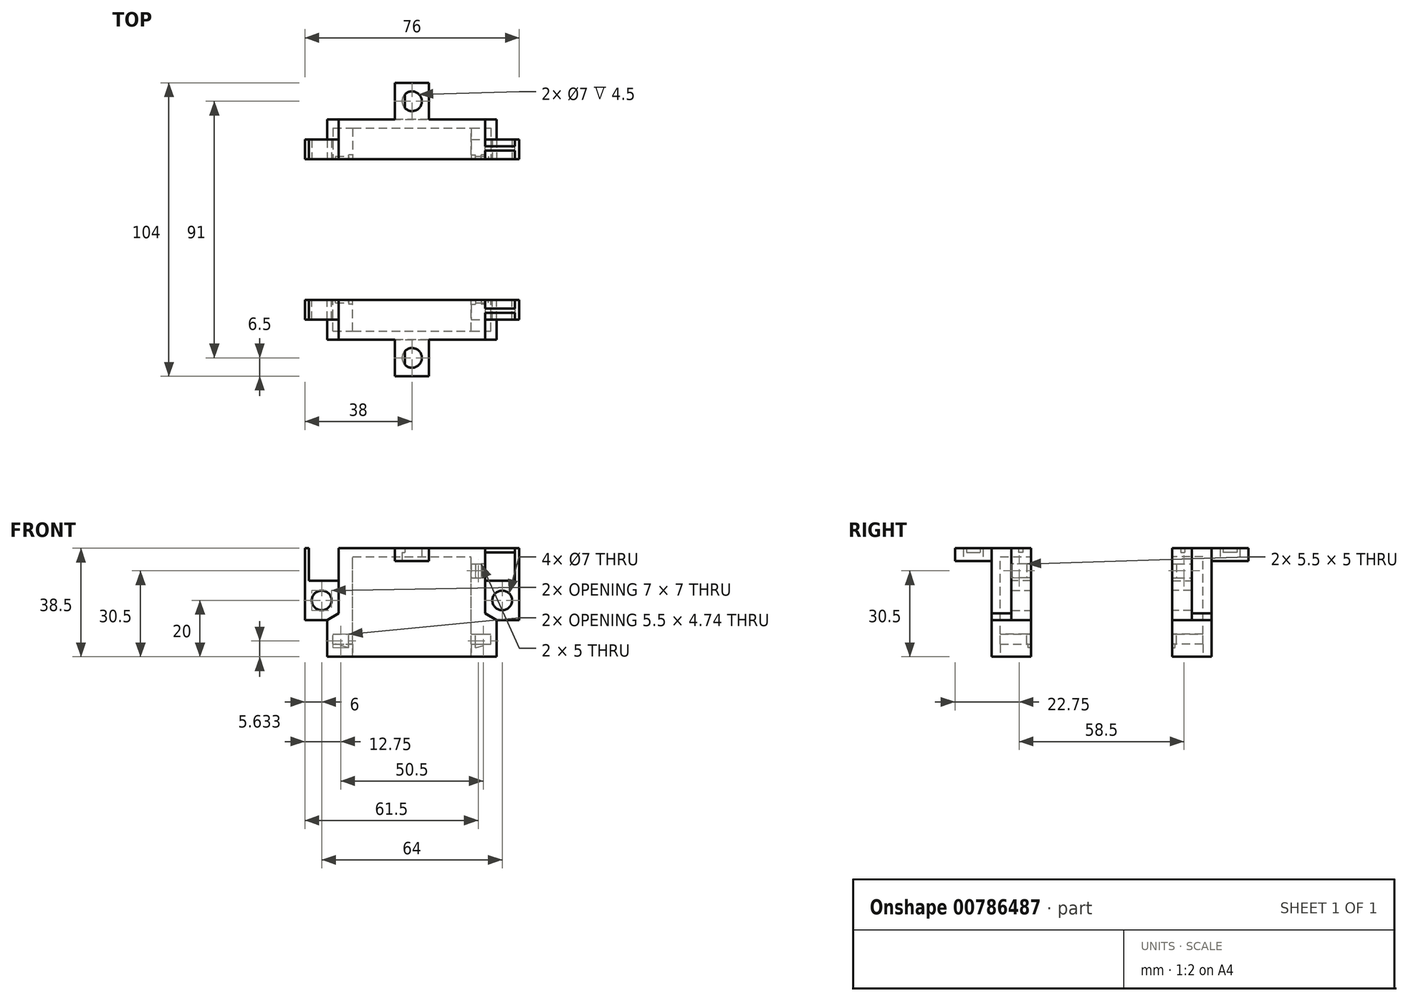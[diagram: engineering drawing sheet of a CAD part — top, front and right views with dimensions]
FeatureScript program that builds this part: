
annotation { "Feature Type Name" : "Feature", "Feature Type Description" : "" }
export const myFeature = defineFeature(function(context is Context, id is Id, definition is map)
    precondition{}
    {
        {
            var Q0;
            Q0=qCreatedBy(makeId("Top.planeOp"),FACE);
            var sketch = newSketch(context, id + "F0", { "sketchPlane" : qUnion([Q0])});
            skLineSegment(sketch, "E0.bottom", {"start": v(-30, 7) * mm, "end": v(30, 7) * mm});
            skLineSegment(sketch, "E0.top", {"start": v(-30, -7) * mm, "end": v(30, -7) * mm});
            skLineSegment(sketch, "E0.left", {"start": v(-30, 7) * mm, "end": v(-30, -7) * mm});
            skLineSegment(sketch, "E0.right", {"start": v(30, 7) * mm, "end": v(30, -7) * mm});
            skSolve(sketch);
        }
        {
            var Q0;
            Q0=qSketchRegion(id+"F0",true);
            extrude(context, id + "F1", {"entities" : qUnion([Q0]), "depth" : 36 * mm, "offsetDistance" : 25 * mm});
        }
        {
            var Q0;
            Q0=makeQuery(id+"F1.opExtrude","CAP_FACE",FACE,{"disambiguationData":[OSD([sQuery(id+"F0.wireOp",EDGE,"E0.bottom"),sQuery(id+"F0.wireOp",EDGE,"E0.top"),sQuery(id+"F0.wireOp",EDGE,"E0.left"),sQuery(id+"F0.wireOp",EDGE,"E0.right")])],"isStart":false});
            cPlane(context, id + "F2", {"entities" : qUnion([Q0]), "cplaneType" : CPlaneType.OFFSET, "offset" : 3 * mm, "oppositeDirection" : true, "width" : 150 * mm, "height" : 150 * mm});
        }
        {
            var Q0;
            Q0=qCreatedBy(id+"F2.planeOp",FACE);
            var sketch = newSketch(context, id + "F3", { "sketchPlane" : qUnion([Q0])});
            skLineSegment(sketch, "E1.bottom", {"start": v(-21, 7) * mm, "end": v(21, 7) * mm});
            skLineSegment(sketch, "E1.top", {"start": v(-21, -4) * mm, "end": v(21, -4) * mm});
            skLineSegment(sketch, "E1.left", {"start": v(-21, 7) * mm, "end": v(-21, -4) * mm});
            skLineSegment(sketch, "E1.right", {"start": v(21, 7) * mm, "end": v(21, -4) * mm});
            skSolve(sketch);
        }
        {
            var Q0;
            Q0=qSketchRegion(id+"F3",true);
            extrude(context, id + "F4", {"entities" : qUnion([Q0]), "operationType" : NewBodyOperationType.REMOVE, "oppositeDirection" : true, "depth" : 25 * mm, "offsetDistance" : 25 * mm});
        }
        {
            var Q0;
            Q0=makeQuery(id+"F1.opExtrude","SWEPT_FACE",FACE,{"disambiguationData":[OSD([sQuery(id+"F0.wireOp",EDGE,"E0.bottom")])]});
            var sketch = newSketch(context, id + "F5", { "sketchPlane" : qUnion([Q0])});
            skLineSegment(sketch, "E2.bottom", {"start": v(28, 4.5) * mm, "end": v(-28, 4.5) * mm});
            skLineSegment(sketch, "E2.top", {"start": v(28, 8) * mm, "end": v(-28, 8) * mm});
            skLineSegment(sketch, "E2.left", {"start": v(28, 4.5) * mm, "end": v(28, 8) * mm});
            skLineSegment(sketch, "E2.right", {"start": v(-28, 4.5) * mm, "end": v(-28, 8) * mm});
            skLineSegment(sketch, "E3.bottom", {"start": v(21, 4.5) * mm, "end": v(-21, 4.5) * mm});
            skLineSegment(sketch, "E3.top", {"start": v(21, 0) * mm, "end": v(-21, 0) * mm});
            skLineSegment(sketch, "E3.left", {"start": v(21, 4.5) * mm, "end": v(21, 0) * mm});
            skLineSegment(sketch, "E3.right", {"start": v(-21, 4.5) * mm, "end": v(-21, 0) * mm});
            skSolve(sketch);
        }
        {
            var Q0;
            {var subQ9=sQuery(id+"F5.wireOp",EDGE,"E2.left");Q0=qUnion([makeQuery(id+"F5.imprint","IMPRINT",FACE,{"disambiguationData":[TD([[makeQuery(id+"F5.imprint","IMPRINT",EDGE,{"derivedFrom":subQ9}),1.0]])]}),makeQuery(id+"F5.imprint","IMPRINT",FACE,{"disambiguationData":[TD([[makeQuery(id+"F5.imprint","IMPRINT",EDGE,{"derivedFrom":sQuery(id+"F5.wireOp",EDGE,"E3.top")}),-1.0]])]})]);}
            extrude(context, id + "F6", {"entities" : qUnion([Q0]), "operationType" : NewBodyOperationType.REMOVE, "oppositeDirection" : true, "depth" : 11 * mm, "offsetDistance" : 25 * mm});
        }
        {
            var Q0;
            Q0=makeQuery(id+"F1.opExtrude","SWEPT_FACE",FACE,{"disambiguationData":[OSD([sQuery(id+"F0.wireOp",EDGE,"E0.bottom")])]});
            var sketch = newSketch(context, id + "F7", { "sketchPlane" : qUnion([Q0])});
            skLineSegment(sketch, "E4.bottom", {"start": v(30, 13) * mm, "end": v(38, 13) * mm});
            skLineSegment(sketch, "E4.top", {"start": v(30, 27) * mm, "end": v(38, 27) * mm});
            skLineSegment(sketch, "E4.left", {"start": v(30, 13) * mm, "end": v(30, 27) * mm});
            skLineSegment(sketch, "E4.right", {"start": v(38, 13) * mm, "end": v(38, 27) * mm});
            skLineSegment(sketch, "E5.MirrorCS", {"start": v(-38, 13) * mm, "end": v(-38, 27) * mm});
            skLineSegment(sketch, "E6.MirrorCS", {"start": v(-30, 13) * mm, "end": v(-38, 13) * mm});
            skLineSegment(sketch, "E7.MirrorCS", {"start": v(-30, 13) * mm, "end": v(-30, 27) * mm});
            skLineSegment(sketch, "E8.MirrorCS", {"start": v(-30, 27) * mm, "end": v(-38, 27) * mm});
            skSolve(sketch);
        }
        {
            var Q0;
            Q0=qSketchRegion(id+"F7",true);
            extrude(context, id + "F8", {"entities" : qUnion([Q0]), "operationType" : NewBodyOperationType.ADD, "oppositeDirection" : true, "depth" : 14 * mm, "offsetDistance" : 25 * mm});
        }
        {
            var Q0;
            Q0=makeQuery(id+"F8.boolean.opBoolean","MERGE",FACE,{"derivedFrom":[makeQuery(id+"F1.opExtrude","SWEPT_FACE",FACE,{"disambiguationData":[OSD([sQuery(id+"F0.wireOp",EDGE,"E0.bottom")])]}),makeQuery(id+"F8.opExtrude","CAP_FACE",FACE,{"disambiguationData":[OSD([sQuery(id+"F7.wireOp",EDGE,"E4.bottom"),sQuery(id+"F7.wireOp",EDGE,"E4.top"),sQuery(id+"F7.wireOp",EDGE,"E4.left"),sQuery(id+"F7.wireOp",EDGE,"E4.right")])],"isStart":true}),makeQuery(id+"F8.opExtrude","CAP_FACE",FACE,{"disambiguationData":[OSD([sQuery(id+"F7.wireOp",EDGE,"E5.MirrorCS"),sQuery(id+"F7.wireOp",EDGE,"E6.MirrorCS"),sQuery(id+"F7.wireOp",EDGE,"E7.MirrorCS"),sQuery(id+"F7.wireOp",EDGE,"E8.MirrorCS")])],"isStart":true})]});
            var sketch = newSketch(context, id + "F9", { "sketchPlane" : qUnion([Q0])});
            skCircle(sketch, "E9", {"center": v(32, 20) * mm, "radius": 3.5 * mm});
            skCircle(sketch, "E10.MirrorC", {"center": v(-32, 20) * mm, "radius": 3.5 * mm});
            skSolve(sketch);
        }
        {
            var Q0;
            Q0=qSketchRegion(id+"F9",true);
            extrude(context, id + "F10", {"entities" : qUnion([Q0]), "operationType" : NewBodyOperationType.REMOVE, "oppositeDirection" : true, "depth" : 14 * mm, "offsetDistance" : 25 * mm});
        }
        {
            var Q0;
            Q0=makeQuery(id+"F8.boolean.opBoolean","MERGE",FACE,{"derivedFrom":[makeQuery(id+"F1.opExtrude","SWEPT_FACE",FACE,{"disambiguationData":[OSD([sQuery(id+"F0.wireOp",EDGE,"E0.top")])]}),makeQuery(id+"F8.opExtrude","CAP_FACE",FACE,{"disambiguationData":[OSD([sQuery(id+"F7.wireOp",EDGE,"E4.bottom"),sQuery(id+"F7.wireOp",EDGE,"E4.top"),sQuery(id+"F7.wireOp",EDGE,"E4.left"),sQuery(id+"F7.wireOp",EDGE,"E4.right")])],"isStart":false}),makeQuery(id+"F8.opExtrude","CAP_FACE",FACE,{"disambiguationData":[OSD([sQuery(id+"F7.wireOp",EDGE,"E5.MirrorCS"),sQuery(id+"F7.wireOp",EDGE,"E6.MirrorCS"),sQuery(id+"F7.wireOp",EDGE,"E7.MirrorCS"),sQuery(id+"F7.wireOp",EDGE,"E8.MirrorCS")])],"isStart":false})]});
            var sketch = newSketch(context, id + "F11", { "sketchPlane" : qUnion([Q0])});
            skLineSegment(sketch, "E11.bottom", {"start": v(38, 13) * mm, "end": v(26, 13) * mm});
            skLineSegment(sketch, "E11.top", {"start": v(38, 27) * mm, "end": v(26, 27) * mm});
            skLineSegment(sketch, "E11.left", {"start": v(38, 13) * mm, "end": v(38, 27) * mm});
            skLineSegment(sketch, "E11.right", {"start": v(26, 13) * mm, "end": v(26, 27) * mm});
            skLineSegment(sketch, "E12.MirrorCS", {"start": v(-38, 13) * mm, "end": v(-26, 13) * mm});
            skLineSegment(sketch, "E13.MirrorCS", {"start": v(-26, 13) * mm, "end": v(-26, 27) * mm});
            skLineSegment(sketch, "E14.MirrorCS", {"start": v(-38, 13) * mm, "end": v(-38, 27) * mm});
            skLineSegment(sketch, "E15.MirrorCS", {"start": v(-38, 27) * mm, "end": v(-26, 27) * mm});
            skSolve(sketch);
        }
        {
            var Q0;
            Q0=qSketchRegion(id+"F11",true);
            extrude(context, id + "F12", {"entities" : qUnion([Q0]), "operationType" : NewBodyOperationType.REMOVE, "oppositeDirection" : true, "depth" : 7 * mm, "offsetDistance" : 25 * mm});
        }
        {
            var Q0;
            Q0=makeQuery(id+"F8.boolean.opBoolean","MERGE",FACE,{"derivedFrom":[makeQuery(id+"F1.opExtrude","SWEPT_FACE",FACE,{"disambiguationData":[OSD([sQuery(id+"F0.wireOp",EDGE,"E0.top")])]}),makeQuery(id+"F8.opExtrude","CAP_FACE",FACE,{"disambiguationData":[OSD([sQuery(id+"F7.wireOp",EDGE,"E4.bottom"),sQuery(id+"F7.wireOp",EDGE,"E4.top"),sQuery(id+"F7.wireOp",EDGE,"E4.left"),sQuery(id+"F7.wireOp",EDGE,"E4.right")])],"isStart":false}),makeQuery(id+"F8.opExtrude","CAP_FACE",FACE,{"disambiguationData":[OSD([sQuery(id+"F7.wireOp",EDGE,"E5.MirrorCS"),sQuery(id+"F7.wireOp",EDGE,"E6.MirrorCS"),sQuery(id+"F7.wireOp",EDGE,"E7.MirrorCS"),sQuery(id+"F7.wireOp",EDGE,"E8.MirrorCS")])],"isStart":false})]});
            var sketch = newSketch(context, id + "F13", { "sketchPlane" : qUnion([Q0])});
            skLineSegment(sketch, "E16.bottom", {"start": v(30, 36) * mm, "end": v(26, 36) * mm});
            skLineSegment(sketch, "E16.top", {"start": v(30, 27) * mm, "end": v(26, 27) * mm});
            skLineSegment(sketch, "E16.left", {"start": v(30, 36) * mm, "end": v(30, 27) * mm});
            skLineSegment(sketch, "E16.right", {"start": v(26, 36) * mm, "end": v(26, 27) * mm});
            skLineSegment(sketch, "E17.bottom", {"start": v(-30, 36) * mm, "end": v(-26, 36) * mm});
            skLineSegment(sketch, "E17.top", {"start": v(-30, 27) * mm, "end": v(-26, 27) * mm});
            skLineSegment(sketch, "E17.left", {"start": v(-30, 36) * mm, "end": v(-30, 27) * mm});
            skLineSegment(sketch, "E17.right", {"start": v(-26, 36) * mm, "end": v(-26, 27) * mm});
            skSolve(sketch);
        }
        {
            var Q0;
            Q0=qSketchRegion(id+"F13",true);
            extrude(context, id + "F14", {"entities" : qUnion([Q0]), "operationType" : NewBodyOperationType.REMOVE, "oppositeDirection" : true, "depth" : 14 * mm, "offsetDistance" : 25 * mm});
        }
        {
            var Q0;
            Q0=makeQuery(id+"F14.boolean.opBoolean","MERGE",FACE,{"derivedFrom":[makeQuery(id+"F12.boolean.opBoolean","COPY",FACE,{"derivedFrom":makeQuery(id+"F12.opExtrude","SWEPT_FACE",FACE,{"disambiguationData":[OSD([sQuery(id+"F11.wireOp",EDGE,"E11.right")])]})}),makeQuery(id+"F14.opExtrude","SWEPT_FACE",FACE,{"disambiguationData":[OSD([sQuery(id+"F13.wireOp",EDGE,"E16.right")])]})]});
            var sketch = newSketch(context, id + "F15", { "sketchPlane" : qUnion([Q0])});
            skLineSegment(sketch, "E18.bottom", {"start": v(7, 33) * mm, "end": v(0, 33) * mm});
            skLineSegment(sketch, "E18.top", {"start": v(7, 28) * mm, "end": v(0, 28) * mm});
            skLineSegment(sketch, "E18.left", {"start": v(7, 33) * mm, "end": v(7, 28) * mm});
            skLineSegment(sketch, "E18.right", {"start": v(0, 33) * mm, "end": v(0, 28) * mm});
            skSolve(sketch);
        }
        {
            var Q0;
            Q0=qSketchRegion(id+"F15",true);
            extrude(context, id + "F16", {"entities" : qUnion([Q0]), "operationType" : NewBodyOperationType.REMOVE, "oppositeDirection" : true, "depth" : 5 * mm, "offsetDistance" : 25 * mm});
        }
        {
            var Q0;
            {var subQ0=sQuery(id+"F7.wireOp",EDGE,"E8.MirrorCS");var subQ1=sQuery(id+"F7.wireOp",EDGE,"E5.MirrorCS");var subQ3=sQuery(id+"F0.wireOp",EDGE,"E0.bottom");var subQ4=makeQuery(id+"F1.opExtrude","SWEPT_FACE",FACE,{"disambiguationData":[OSD([subQ3])]});var subQ10=sQuery(id+"F0.wireOp",EDGE,"E0.right");var subQ11=sQuery(id+"F7.wireOp",EDGE,"E6.MirrorCS");Q0=makeQuery(id+"F16.boolean.opBoolean","SPLIT",FACE,{"disambiguationData":[TD([makeQuery(id+"F1.opExtrude","SWEPT_FACE",FACE,{"disambiguationData":[OSD([subQ10])]})])],"derivedFrom":makeQuery(id+"F8.boolean.opBoolean","MERGE",FACE,{"derivedFrom":[subQ4,makeQuery(id+"F8.opExtrude","CAP_FACE",FACE,{"disambiguationData":[OSD([sQuery(id+"F7.wireOp",EDGE,"E4.bottom"),sQuery(id+"F7.wireOp",EDGE,"E4.top"),sQuery(id+"F7.wireOp",EDGE,"E4.left"),sQuery(id+"F7.wireOp",EDGE,"E4.right")])],"isStart":true}),makeQuery(id+"F8.opExtrude","CAP_FACE",FACE,{"disambiguationData":[OSD([subQ1,subQ11,sQuery(id+"F7.wireOp",EDGE,"E7.MirrorCS"),subQ0])],"isStart":true})]})});}
            var sketch = newSketch(context, id + "F17", { "sketchPlane" : qUnion([Q0])});
            skLineSegment(sketch, "E19", {"start": v(-21, 2.86) * mm, "end": v(-27.1, 4.5) * mm});
            skLineSegment(sketch, "E20", {"start": v(-27.1, 4.5) * mm, "end": v(-21, 4.5) * mm});
            skLineSegment(sketch, "E21", {"start": v(-21, 4.5) * mm, "end": v(-21, 2.86) * mm});
            skLineSegment(sketch, "E22.MirrorCS", {"start": v(21, 2.86) * mm, "end": v(27.1, 4.5) * mm});
            skLineSegment(sketch, "E23.MirrorCS", {"start": v(21, 4.5) * mm, "end": v(21, 2.86) * mm});
            skLineSegment(sketch, "E24.MirrorCS", {"start": v(27.1, 4.5) * mm, "end": v(21, 4.5) * mm});
            skSolve(sketch);
        }
        {
            var Q0;
            Q0=qSketchRegion(id+"F17",true);
            extrude(context, id + "F18", {"entities" : qUnion([Q0]), "operationType" : NewBodyOperationType.REMOVE, "oppositeDirection" : true, "depth" : 1 * mm, "offsetDistance" : 25 * mm});
        }
        {
            var Q0;
            Q0=makeQuery(id+"F8.boolean.opBoolean","MERGE",FACE,{"derivedFrom":[makeQuery(id+"F1.opExtrude","SWEPT_FACE",FACE,{"disambiguationData":[OSD([sQuery(id+"F0.wireOp",EDGE,"E0.top")])]}),makeQuery(id+"F8.opExtrude","CAP_FACE",FACE,{"disambiguationData":[OSD([sQuery(id+"F7.wireOp",EDGE,"E4.bottom"),sQuery(id+"F7.wireOp",EDGE,"E4.top"),sQuery(id+"F7.wireOp",EDGE,"E4.left"),sQuery(id+"F7.wireOp",EDGE,"E4.right")])],"isStart":false}),makeQuery(id+"F8.opExtrude","CAP_FACE",FACE,{"disambiguationData":[OSD([sQuery(id+"F7.wireOp",EDGE,"E5.MirrorCS"),sQuery(id+"F7.wireOp",EDGE,"E6.MirrorCS"),sQuery(id+"F7.wireOp",EDGE,"E7.MirrorCS"),sQuery(id+"F7.wireOp",EDGE,"E8.MirrorCS")])],"isStart":false})]});
            var sketch = newSketch(context, id + "F19", { "sketchPlane" : qUnion([Q0])});
            skLineSegment(sketch, "E25.bottom", {"start": v(6, 36) * mm, "end": v(-6, 36) * mm});
            skLineSegment(sketch, "E25.top", {"start": v(6, 31) * mm, "end": v(-6, 31) * mm});
            skLineSegment(sketch, "E25.left", {"start": v(6, 36) * mm, "end": v(6, 31) * mm});
            skLineSegment(sketch, "E25.right", {"start": v(-6, 36) * mm, "end": v(-6, 31) * mm});
            skSolve(sketch);
        }
        {
            var Q0;
            Q0=qSketchRegion(id+"F19",true);
            extrude(context, id + "F20", {"entities" : qUnion([Q0]), "operationType" : NewBodyOperationType.ADD, "depth" : 13 * mm, "offsetDistance" : 25 * mm});
        }
        {
            var Q0;
            Q0=makeQuery(id+"F20.opExtrude","SWEPT_FACE",FACE,{"disambiguationData":[OSD([sQuery(id+"F19.wireOp",EDGE,"E25.top")])]});
            var sketch = newSketch(context, id + "F21", { "sketchPlane" : qUnion([Q0])});
            skCircle(sketch, "E26", {"center": v(0, 13.5) * mm, "radius": 3.5 * mm});
            skPoint(sketch, "E26.centerSnap0", {"position": v(6, 13.5) * mm});
            skSolve(sketch);
        }
        {
            var Q0;
            Q0=qSketchRegion(id+"F21",true);
            extrude(context, id + "F22", {"entities" : qUnion([Q0]), "operationType" : NewBodyOperationType.REMOVE, "oppositeDirection" : true, "depth" : 5 * mm, "offsetDistance" : 25 * mm});
        }
        {
            var Q0;
            {var subQ0=sQuery(id+"F7.wireOp",EDGE,"E8.MirrorCS");var subQ1=sQuery(id+"F7.wireOp",EDGE,"E5.MirrorCS");var subQ3=sQuery(id+"F0.wireOp",EDGE,"E0.bottom");var subQ4=makeQuery(id+"F1.opExtrude","SWEPT_FACE",FACE,{"disambiguationData":[OSD([subQ3])]});var subQ10=sQuery(id+"F0.wireOp",EDGE,"E0.right");var subQ11=sQuery(id+"F7.wireOp",EDGE,"E6.MirrorCS");Q0=makeQuery(id+"F16.boolean.opBoolean","SPLIT",FACE,{"disambiguationData":[TD([makeQuery(id+"F1.opExtrude","SWEPT_FACE",FACE,{"disambiguationData":[OSD([subQ10])]})])],"derivedFrom":makeQuery(id+"F8.boolean.opBoolean","MERGE",FACE,{"derivedFrom":[subQ4,makeQuery(id+"F8.opExtrude","CAP_FACE",FACE,{"disambiguationData":[OSD([sQuery(id+"F7.wireOp",EDGE,"E4.bottom"),sQuery(id+"F7.wireOp",EDGE,"E4.top"),sQuery(id+"F7.wireOp",EDGE,"E4.left"),sQuery(id+"F7.wireOp",EDGE,"E4.right")])],"isStart":true}),makeQuery(id+"F8.opExtrude","CAP_FACE",FACE,{"disambiguationData":[OSD([subQ1,subQ11,sQuery(id+"F7.wireOp",EDGE,"E7.MirrorCS"),subQ0])],"isStart":true})]})});}
            cPlane(context, id + "F23", {"entities" : qUnion([Q0]), "cplaneType" : CPlaneType.OFFSET, "offset" : 25 * mm, "width" : 150 * mm, "height" : 150 * mm});
        }
        {
            var Q0;
            {var subQ0=sQuery(id+"F7.wireOp",EDGE,"E8.MirrorCS");var subQ1=sQuery(id+"F7.wireOp",EDGE,"E5.MirrorCS");var subQ3=sQuery(id+"F0.wireOp",EDGE,"E0.bottom");var subQ4=makeQuery(id+"F1.opExtrude","SWEPT_FACE",FACE,{"disambiguationData":[OSD([subQ3])]});var subQ10=sQuery(id+"F0.wireOp",EDGE,"E0.right");var subQ11=sQuery(id+"F7.wireOp",EDGE,"E6.MirrorCS");Q0=makeQuery(id+"F16.boolean.opBoolean","SPLIT",FACE,{"disambiguationData":[TD([makeQuery(id+"F1.opExtrude","SWEPT_FACE",FACE,{"disambiguationData":[OSD([subQ10])]})])],"derivedFrom":makeQuery(id+"F8.boolean.opBoolean","MERGE",FACE,{"derivedFrom":[subQ4,makeQuery(id+"F8.opExtrude","CAP_FACE",FACE,{"disambiguationData":[OSD([sQuery(id+"F7.wireOp",EDGE,"E4.bottom"),sQuery(id+"F7.wireOp",EDGE,"E4.top"),sQuery(id+"F7.wireOp",EDGE,"E4.left"),sQuery(id+"F7.wireOp",EDGE,"E4.right")])],"isStart":true}),makeQuery(id+"F8.opExtrude","CAP_FACE",FACE,{"disambiguationData":[OSD([subQ1,subQ11,sQuery(id+"F7.wireOp",EDGE,"E7.MirrorCS"),subQ0])],"isStart":true})]})});}
            var sketch = newSketch(context, id + "F24", { "sketchPlane" : qUnion([Q0])});
            skSolve(sketch);
        }
        {
            var Q0;
            {var subQ13=sQuery(id+"F5.wireOp",EDGE,"E2.right");Q0=makeQuery(id+"F24.imprint","IMPRINT",FACE,{"disambiguationData":[TD([[makeQuery(id+"F24.imprint","IMPRINT",EDGE,{"derivedFrom":makeQuery(id+"F6.boolean.opBoolean","COPY",EDGE,{"derivedFrom":makeQuery(id+"F6.opExtrude","CAP_EDGE",EDGE,{"disambiguationData":[OSD([subQ13])],"isStart":true})})}),1.0]])]});}
            var sketch = newSketch(context, id + "F25", { "sketchPlane" : qUnion([Q0])});
            skLineSegment(sketch, "E27", {"start": v(-20.97, 30.16) * mm, "end": v(-20.97, 10.16) * mm});
            skLineSegment(sketch, "E28", {"start": v(-17.97, 38.1) * mm, "end": v(-17.97, 0) * mm});
            skLineSegment(sketch, "E29", {"start": v(-20.97, 30.16) * mm, "end": v(-20.97, 38.05) * mm});
            skLineSegment(sketch, "E30", {"start": v(-20.97, 10.16) * mm, "end": v(-20.97, 0) * mm});
            skLineSegment(sketch, "E31", {"start": v(-27.97, 10) * mm, "end": v(-27.97, 6.63) * mm});
            skLineSegment(sketch, "E32", {"start": v(-27.03, 6.47) * mm, "end": v(-27.03, 0) * mm});
            skSolve(sketch);
        }
        {
            var Q0;
            Q0=makeQuery(id+"F20.boolean.opBoolean","MERGE",FACE,{"derivedFrom":[makeQuery(id+"F1.opExtrude","CAP_FACE",FACE,{"disambiguationData":[OSD([sQuery(id+"F0.wireOp",EDGE,"E0.bottom"),sQuery(id+"F0.wireOp",EDGE,"E0.top"),sQuery(id+"F0.wireOp",EDGE,"E0.left"),sQuery(id+"F0.wireOp",EDGE,"E0.right")])],"isStart":false}),makeQuery(id+"F20.opExtrude","SWEPT_FACE",FACE,{"disambiguationData":[OSD([sQuery(id+"F19.wireOp",EDGE,"E25.bottom")])]})]});
            extrude(context, id + "F26", {"entities" : qUnion([Q0]), "operationType" : NewBodyOperationType.ADD, "depth" : 2.5 * mm, "offsetDistance" : 25 * mm});
        }
        {
            var Q0;
            {var subQ0=sQuery(id+"F0.wireOp",EDGE,"E0.bottom");var subQ9=makeQuery(id+"F1.opExtrude","SWEPT_FACE",FACE,{"disambiguationData":[OSD([subQ0])]});var subQ10=sQuery(id+"F7.wireOp",EDGE,"E4.right");var subQ12=sQuery(id+"F0.wireOp",EDGE,"E0.left");var subQ14=sQuery(id+"F7.wireOp",EDGE,"E4.bottom");var subQ15=sQuery(id+"F7.wireOp",EDGE,"E4.top");Q0=makeQuery(id+"F26.boolean.opBoolean","MERGE",FACE,{"derivedFrom":[makeQuery(id+"F16.boolean.opBoolean","SPLIT",FACE,{"disambiguationData":[TD([makeQuery(id+"F1.opExtrude","SWEPT_FACE",FACE,{"disambiguationData":[OSD([subQ12])]})])],"derivedFrom":makeQuery(id+"F8.boolean.opBoolean","MERGE",FACE,{"derivedFrom":[subQ9,makeQuery(id+"F8.opExtrude","CAP_FACE",FACE,{"disambiguationData":[OSD([subQ14,subQ15,sQuery(id+"F7.wireOp",EDGE,"E4.left"),subQ10])],"isStart":true}),makeQuery(id+"F8.opExtrude","CAP_FACE",FACE,{"disambiguationData":[OSD([sQuery(id+"F7.wireOp",EDGE,"E5.MirrorCS"),sQuery(id+"F7.wireOp",EDGE,"E6.MirrorCS"),sQuery(id+"F7.wireOp",EDGE,"E7.MirrorCS"),sQuery(id+"F7.wireOp",EDGE,"E8.MirrorCS")])],"isStart":true})]})}),makeQuery(id+"F26.opExtrude","SWEPT_FACE",FACE,{"disambiguationData":[OSD([subQ0])]})]});}
            var sketch = newSketch(context, id + "F27", { "sketchPlane" : qUnion([Q0])});
            skLineSegment(sketch, "E33.bottom", {"start": v(21, 33) * mm, "end": v(-21, 33) * mm});
            skLineSegment(sketch, "E33.top", {"start": v(21, 35.5) * mm, "end": v(-21, 35.5) * mm});
            skLineSegment(sketch, "E33.left", {"start": v(21, 33) * mm, "end": v(21, 35.5) * mm});
            skLineSegment(sketch, "E33.right", {"start": v(-21, 33) * mm, "end": v(-21, 35.5) * mm});
            skSolve(sketch);
        }
        {
            var Q0;
            Q0 = qSketchRegion(id + "F27", true);
            extrude(context, id + "F28", {"entities" : qUnion([Q0]), "operationType" : NewBodyOperationType.REMOVE, "oppositeDirection" : true, "depth" : 11 * mm, "offsetDistance" : 25 * mm});
        }
        {
            var Q0;
            Q0=makeQuery(id+"F20.opExtrude","SWEPT_FACE",FACE,{"disambiguationData":[OSD([sQuery(id+"F19.wireOp",EDGE,"E25.top")])]});
            extrude(context, id + "F29", {"entities" : qUnion([Q0]), "operationType" : NewBodyOperationType.REMOVE, "oppositeDirection" : true, "depth" : 3 * mm, "offsetDistance" : 25 * mm});
        }
        {
            var Q0;
            Q0=makeQuery(id+"F14.boolean.opBoolean","MERGE",FACE,{"derivedFrom":[makeQuery(id+"F8.opExtrude","SWEPT_FACE",FACE,{"disambiguationData":[OSD([sQuery(id+"F7.wireOp",EDGE,"E8.MirrorCS")])]})],"fromTools":[makeQuery(id+"F14.opExtrude","SWEPT_FACE",FACE,{"disambiguationData":[OSD([sQuery(id+"F13.wireOp",EDGE,"E16.top")])]})]});
            var sketch = newSketch(context, id + "F30", { "sketchPlane" : qUnion([Q0])});
            skLineSegment(sketch, "E34.bottom", {"start": v(38, 7) * mm, "end": v(36.5, 7) * mm});
            skLineSegment(sketch, "E34.top", {"start": v(38, 0) * mm, "end": v(36.5, 0) * mm});
            skLineSegment(sketch, "E34.left", {"start": v(38, 7) * mm, "end": v(38, 0) * mm});
            skLineSegment(sketch, "E34.right", {"start": v(36.5, 7) * mm, "end": v(36.5, 0) * mm});
            skLineSegment(sketch, "E35.MirrorCS", {"start": v(-36.5, 7) * mm, "end": v(-36.5, 0) * mm});
            skLineSegment(sketch, "E36.MirrorCS", {"start": v(-38, 0) * mm, "end": v(-36.5, 0) * mm});
            skLineSegment(sketch, "E37.MirrorCS", {"start": v(-38, 7) * mm, "end": v(-38, 0) * mm});
            skLineSegment(sketch, "E38.MirrorCS", {"start": v(-38, 7) * mm, "end": v(-36.5, 7) * mm});
            skSolve(sketch);
        }
        {
            var Q0;
            Q0 = qSketchRegion(id + "F30", true);
            extrude(context, id + "F31", {"entities" : qUnion([Q0]), "operationType" : NewBodyOperationType.ADD, "depth" : 11.5 * mm, "offsetDistance" : 25 * mm});
        }
        {
            var Q0;
            Q0=makeQuery(id+"F16.boolean.opBoolean","COPY",FACE,{"derivedFrom":makeQuery(id+"F16.opExtrude","SWEPT_FACE",FACE,{"disambiguationData":[OSD([sQuery(id+"F15.wireOp",EDGE,"E18.top")])]})});
            var sketch = newSketch(context, id + "F32", { "sketchPlane" : qUnion([Q0])});
            skPoint(sketch, "E39.oppositeSnap0", {"position": v(24.5, 0) * mm});
            skLineSegment(sketch, "E39.bottom", {"start": v(26, 7) * mm, "end": v(24.5, 7) * mm});
            skLineSegment(sketch, "E39.top", {"start": v(26, 5.5) * mm, "end": v(24.5, 5.5) * mm});
            skLineSegment(sketch, "E39.left", {"start": v(26, 7) * mm, "end": v(26, 5.5) * mm});
            skLineSegment(sketch, "E39.right", {"start": v(24.5, 7) * mm, "end": v(24.5, 5.5) * mm});
            skLineSegment(sketch, "E40.bottom", {"start": v(21, 7) * mm, "end": v(22.5, 7) * mm});
            skLineSegment(sketch, "E40.top", {"start": v(21, 5.5) * mm, "end": v(22.5, 5.5) * mm});
            skLineSegment(sketch, "E40.left", {"start": v(21, 7) * mm, "end": v(21, 5.5) * mm});
            skLineSegment(sketch, "E40.right", {"start": v(22.5, 7) * mm, "end": v(22.5, 5.5) * mm});
            skSolve(sketch);
        }
        {
            var Q0;
            Q0 = qSketchRegion(id + "F32", true);
            extrude(context, id + "F33", {"entities" : qUnion([Q0]), "operationType" : NewBodyOperationType.ADD, "depth" : 5 * mm, "offsetDistance" : 25 * mm});
        }
        {
            var Q0;
            {var subQ1=sQuery(id+"F5.wireOp",EDGE,"E2.top");Q0=makeQuery(id+"F6.boolean.opBoolean","COPY",FACE,{"disambiguationData":[TD([makeQuery(id+"F4.boolean.opBoolean","COPY",FACE,{"derivedFrom":makeQuery(id+"F4.opExtrude","SWEPT_FACE",FACE,{"disambiguationData":[OSD([sQuery(id+"F3.wireOp",EDGE,"E1.right")])]})})])],"derivedFrom":makeQuery(id+"F6.opExtrude","SWEPT_FACE",FACE,{"disambiguationData":[OSD([subQ1])]})});}
            var sketch = newSketch(context, id + "F34", { "sketchPlane" : qUnion([Q0])});
            skLineSegment(sketch, "E41.bottom", {"start": v(21, -7) * mm, "end": v(22.5, -7) * mm});
            skLineSegment(sketch, "E41.top", {"start": v(21, -5.5) * mm, "end": v(22.5, -5.5) * mm});
            skLineSegment(sketch, "E41.left", {"start": v(21, -7) * mm, "end": v(21, -5.5) * mm});
            skLineSegment(sketch, "E41.right", {"start": v(22.5, -7) * mm, "end": v(22.5, -5.5) * mm});
            skLineSegment(sketch, "E42.MirrorCS", {"start": v(-21, -5.5) * mm, "end": v(-22.5, -5.5) * mm});
            skLineSegment(sketch, "E43.MirrorCS", {"start": v(-21, -7) * mm, "end": v(-21, -5.5) * mm});
            skLineSegment(sketch, "E44.MirrorCS", {"start": v(-21, -7) * mm, "end": v(-22.5, -7) * mm});
            skLineSegment(sketch, "E45.MirrorCS", {"start": v(-22.5, -7) * mm, "end": v(-22.5, -5.5) * mm});
            skSolve(sketch);
        }
        {
            var Q0;
            Q0 = qSketchRegion(id + "F34", true);
            extrude(context, id + "F35", {"entities" : qUnion([Q0]), "operationType" : NewBodyOperationType.ADD, "depth" : 6 * mm, "offsetDistance" : 25 * mm});
        }
        {
            var Q0;
            {var subQ0=sQuery(id+"F19.wireOp",EDGE,"E25.top");var subQ1=makeQuery(id+"F8.opExtrude","CAP_FACE",FACE,{"disambiguationData":[OSD([sQuery(id+"F7.wireOp",EDGE,"E5.MirrorCS"),sQuery(id+"F7.wireOp",EDGE,"E6.MirrorCS"),sQuery(id+"F7.wireOp",EDGE,"E7.MirrorCS"),sQuery(id+"F7.wireOp",EDGE,"E8.MirrorCS")])],"isStart":false});var subQ2=makeQuery(id+"F8.opExtrude","CAP_FACE",FACE,{"disambiguationData":[OSD([sQuery(id+"F7.wireOp",EDGE,"E4.bottom"),sQuery(id+"F7.wireOp",EDGE,"E4.top"),sQuery(id+"F7.wireOp",EDGE,"E4.left"),sQuery(id+"F7.wireOp",EDGE,"E4.right")])],"isStart":false});var subQ4=sQuery(id+"F0.wireOp",EDGE,"E0.top");var subQ5=makeQuery(id+"F1.opExtrude","SWEPT_FACE",FACE,{"disambiguationData":[OSD([subQ4])]});var subQ7=makeQuery(id+"F1.opExtrude","CAP_EDGE",EDGE,{"disambiguationData":[OSD([subQ4])],"isStart":false});Q0=makeQuery(id+"F29.boolean.opBoolean","MERGE",FACE,{"derivedFrom":[makeQuery(id+"F26.boolean.opBoolean","MERGE",FACE,{"derivedFrom":[makeQuery(id+"F8.boolean.opBoolean","MERGE",FACE,{"derivedFrom":[subQ5,subQ2,subQ1]}),makeQuery(id+"F26.opExtrude","SWEPT_FACE",FACE,{"disambiguationData":[OSD([subQ4]),TDD([makeQuery(id+"F20.boolean.opBoolean","SPLIT",EDGE,{"disambiguationData":[TD([makeQuery(id+"F12.boolean.opBoolean","COPY",FACE,{"derivedFrom":makeQuery(id+"F12.opExtrude","SWEPT_FACE",FACE,{"disambiguationData":[OSD([sQuery(id+"F11.wireOp",EDGE,"E11.right")])]})})])],"derivedFrom":subQ7})])]}),makeQuery(id+"F26.opExtrude","SWEPT_FACE",FACE,{"disambiguationData":[OSD([subQ4]),TDD([makeQuery(id+"F20.boolean.opBoolean","SPLIT",EDGE,{"disambiguationData":[TD([makeQuery(id+"F12.boolean.opBoolean","COPY",FACE,{"derivedFrom":makeQuery(id+"F12.opExtrude","SWEPT_FACE",FACE,{"disambiguationData":[OSD([sQuery(id+"F11.wireOp",EDGE,"E13.MirrorCS")])]})})])],"derivedFrom":subQ7})])]})]})],"fromTools":[makeQuery(id+"F29.opExtrude","SWEPT_FACE",FACE,{"disambiguationData":[OSD([subQ0]),TDD([makeQuery(id+"F20.opExtrude","CAP_EDGE",EDGE,{"disambiguationData":[OSD([subQ0])],"isStart":true})])]})]});}
            var sketch = newSketch(context, id + "F36", { "sketchPlane" : qUnion([Q0])});
            skLineSegment(sketch, "E46", {"start": v(-26, 15.46) * mm, "end": v(-30, 13) * mm});
            skLineSegment(sketch, "E47", {"start": v(-30, 13) * mm, "end": v(-26, 13) * mm});
            skLineSegment(sketch, "E48", {"start": v(-26, 13) * mm, "end": v(-26, 15.46) * mm});
            skLineSegment(sketch, "E49.MirrorCS", {"start": v(26, 13) * mm, "end": v(26, 15.46) * mm});
            skLineSegment(sketch, "E50.MirrorCS", {"start": v(30, 13) * mm, "end": v(26, 13) * mm});
            skLineSegment(sketch, "E51.MirrorCS", {"start": v(26, 15.46) * mm, "end": v(30, 13) * mm});
            skSolve(sketch);
        }
        {
            var Q0;
            Q0 = qSketchRegion(id + "F36", true);
            extrude(context, id + "F37", {"entities" : qUnion([Q0]), "operationType" : NewBodyOperationType.ADD, "oppositeDirection" : true, "depth" : 7 * mm, "offsetDistance" : 25 * mm});
        }
        {
            var Q0;
            {var subQ0=sQuery(id+"F13.wireOp",EDGE,"E16.right");Q0=makeQuery(id+"F33.boolean.opBoolean","MERGE",FACE,{"derivedFrom":[makeQuery(id+"F26.boolean.opBoolean","MERGE",FACE,{"derivedFrom":[makeQuery(id+"F14.boolean.opBoolean","MERGE",FACE,{"derivedFrom":[makeQuery(id+"F12.boolean.opBoolean","COPY",FACE,{"derivedFrom":makeQuery(id+"F12.opExtrude","SWEPT_FACE",FACE,{"disambiguationData":[OSD([sQuery(id+"F11.wireOp",EDGE,"E11.right")])]})})],"fromTools":[makeQuery(id+"F14.opExtrude","SWEPT_FACE",FACE,{"disambiguationData":[OSD([subQ0])]})]}),makeQuery(id+"F26.opExtrude","SWEPT_FACE",FACE,{"disambiguationData":[OSD([sQuery(id+"F0.wireOp",EDGE,"E0.top"),sQuery(id+"F13.wireOp",EDGE,"E16.bottom"),subQ0])]})]}),makeQuery(id+"F33.opExtrude","SWEPT_FACE",FACE,{"disambiguationData":[OSD([sQuery(id+"F32.wireOp",EDGE,"E39.left")])]})]});}
            var sketch = newSketch(context, id + "F38", { "sketchPlane" : qUnion([Q0])});
            skLineSegment(sketch, "E52.bottom", {"start": v(4, 38.5) * mm, "end": v(2.5, 38.5) * mm});
            skLineSegment(sketch, "E52.top", {"start": v(4, 37) * mm, "end": v(2.5, 37) * mm});
            skLineSegment(sketch, "E52.left", {"start": v(4, 38.5) * mm, "end": v(4, 37) * mm});
            skLineSegment(sketch, "E52.right", {"start": v(2.5, 38.5) * mm, "end": v(2.5, 37) * mm});
            skSolve(sketch);
        }
        {
            var Q0;
            Q0 = qSketchRegion(id + "F38", true);
            extrude(context, id + "F39", {"entities" : qUnion([Q0]), "operationType" : NewBodyOperationType.ADD, "depth" : 11 * mm, "offsetDistance" : 25 * mm});
        }
        {
            var Q0;
            {var subQ0=sQuery(id+"F13.wireOp",EDGE,"E17.right");Q0=makeQuery(id+"F26.boolean.opBoolean","MERGE",FACE,{"derivedFrom":[makeQuery(id+"F14.boolean.opBoolean","MERGE",FACE,{"derivedFrom":[makeQuery(id+"F12.boolean.opBoolean","COPY",FACE,{"derivedFrom":makeQuery(id+"F12.opExtrude","SWEPT_FACE",FACE,{"disambiguationData":[OSD([sQuery(id+"F11.wireOp",EDGE,"E13.MirrorCS")])]})})],"fromTools":[makeQuery(id+"F14.opExtrude","SWEPT_FACE",FACE,{"disambiguationData":[OSD([subQ0])]})]}),makeQuery(id+"F26.opExtrude","SWEPT_FACE",FACE,{"disambiguationData":[OSD([sQuery(id+"F0.wireOp",EDGE,"E0.top"),sQuery(id+"F13.wireOp",EDGE,"E17.bottom"),subQ0])]})]});}
            var sketch = newSketch(context, id + "F40", { "sketchPlane" : qUnion([Q0])});
            skLineSegment(sketch, "E53.bottom", {"start": v(-2.5, 38.5) * mm, "end": v(-4, 38.5) * mm});
            skLineSegment(sketch, "E53.top", {"start": v(-2.5, 37) * mm, "end": v(-4, 37) * mm});
            skLineSegment(sketch, "E53.left", {"start": v(-2.5, 38.5) * mm, "end": v(-2.5, 37) * mm});
            skLineSegment(sketch, "E53.right", {"start": v(-4, 38.5) * mm, "end": v(-4, 37) * mm});
            skSolve(sketch);
        }
        {
            var Q0;
            Q0 = qSketchRegion(id + "F40", true);
            extrude(context, id + "F41", {"entities" : qUnion([Q0]), "operationType" : NewBodyOperationType.ADD, "depth" : 11 * mm, "offsetDistance" : 25 * mm});
        }
        {
            var Q0;
            Q0=makeQuery(id+"F1.opExtrude","SWEPT_BODY",BODY,{"disambiguationData":[OSD([sQuery(id+"F0.wireOp",EDGE,"E0.bottom"),sQuery(id+"F0.wireOp",EDGE,"E0.top"),sQuery(id+"F0.wireOp",EDGE,"E0.left"),sQuery(id+"F0.wireOp",EDGE,"E0.right")])]});
            var Q1;
            Q1=qCreatedBy(id+"F23.planeOp",FACE);
            mirror(context, id + "F42", {"entities" : qUnion([Q0]), "mirrorPlane" : qUnion([Q1])});
        }
    });
